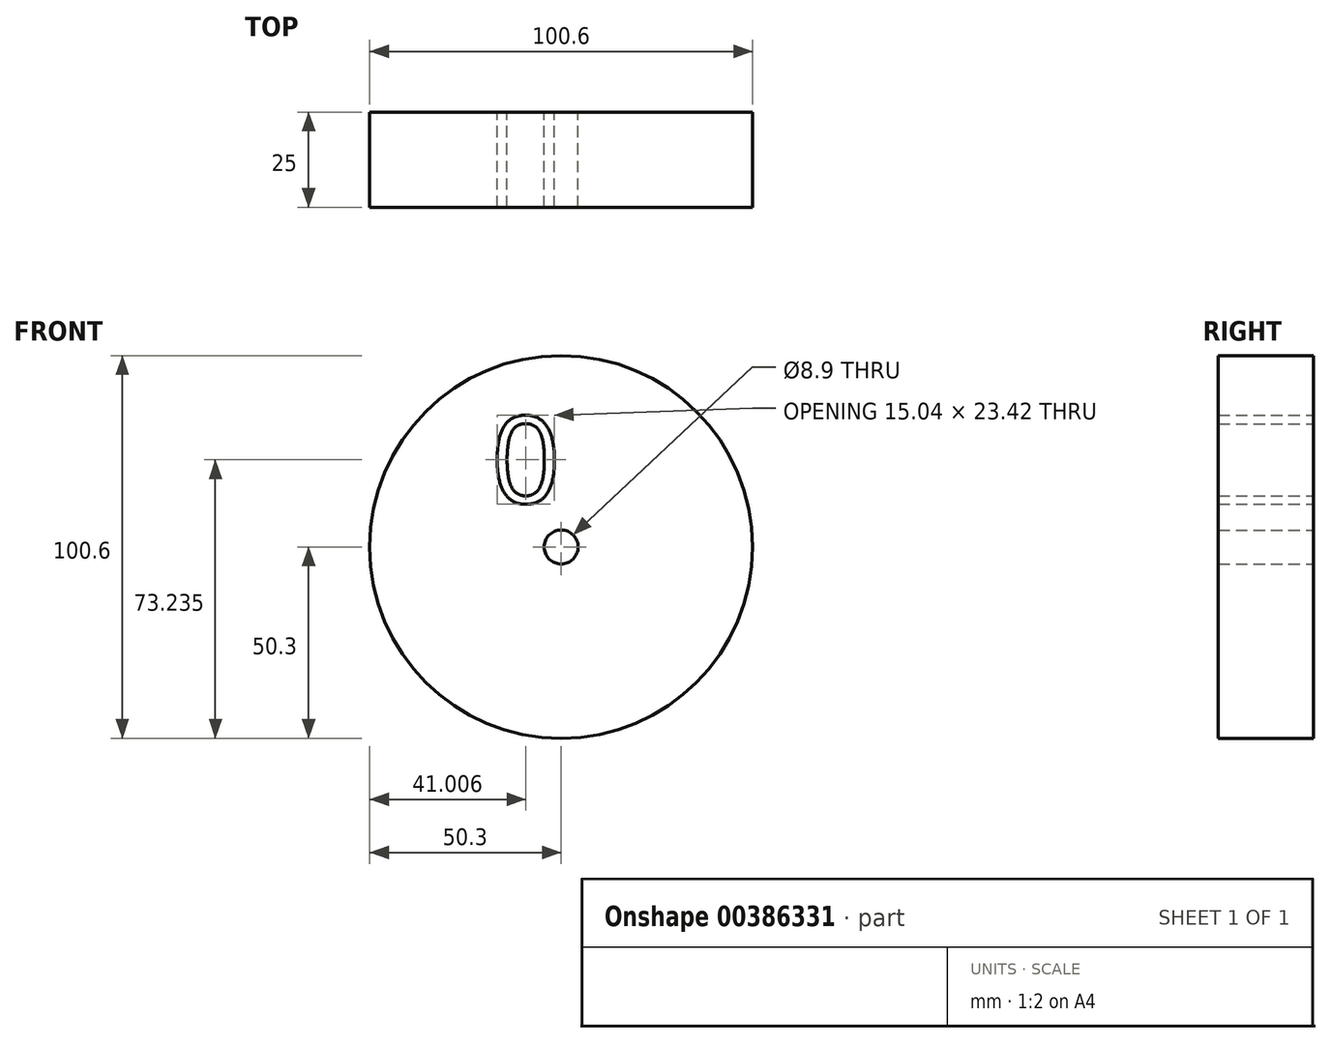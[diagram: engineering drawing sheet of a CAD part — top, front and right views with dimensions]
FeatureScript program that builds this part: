
annotation { "Feature Type Name" : "Feature", "Feature Type Description" : "" }
export const myFeature = defineFeature(function(context is Context, id is Id, definition is map)
    precondition{}
    {
        {
            var Q0;
            Q0=qCreatedBy(makeId("Front.planeOp"),FACE);
            var sketch = newSketch(context, id + "F0", { "sketchPlane" : qUnion([Q0])});
            skCircle(sketch, "E0", {"center": v(0, 0) * mm, "radius": 50.3 * mm});
            skCircle(sketch, "E1", {"center": v(0, 0) * mm, "radius": 4.45 * mm});
            skText(sketch, "E2", { "text": "2017", "fontName": "OpenSans-Regular.ttf"});
            const initialGuessF0  = {"E2": [-0.03662, 0.01154, 1, 0, 0.02294]};
            skSetInitialGuess(sketch, initialGuessF0);
            skSolve(sketch);
        }
        {
            var Q0;
            Q0 = qSketchRegion(id + "F0", true);
            var Q1;
            Q1=makeQuery(id+"F0.imprint","IMPRINT",FACE,{"disambiguationData":[TD([[makeQuery(id+"F0.imprint","IMPRINT",EDGE,{"derivedFrom":sQuery(id+"F0.wireOp",EDGE,"E2.sketch_text.stroke-0")}),-1.0]])]});
            var Q2;
            Q2=makeQuery(id+"F0.imprint","IMPRINT",FACE,{"disambiguationData":[TD([[makeQuery(id+"F0.imprint","IMPRINT",EDGE,{"derivedFrom":sQuery(id+"F0.wireOp",EDGE,"E2.sketch_text.stroke-28")}),1.0]])]});
            var Q3;
            Q3=makeQuery(id+"F0.imprint","IMPRINT",FACE,{"disambiguationData":[TD([[makeQuery(id+"F0.imprint","IMPRINT",EDGE,{"derivedFrom":sQuery(id+"F0.wireOp",EDGE,"E2.sketch_text.stroke-36")}),-1.0]])]});
            var Q4;
            Q4=makeQuery(id+"F0.imprint","IMPRINT",FACE,{"disambiguationData":[TD([[makeQuery(id+"F0.imprint","IMPRINT",EDGE,{"derivedFrom":sQuery(id+"F0.wireOp",EDGE,"E2.sketch_text.stroke-45")}),-1.0]])]});
            extrude(context, id + "F1", {"entities" : qUnion([Q0, Q1, Q2, Q3, Q4]), "depth" : 25 * mm});
        }
    });
